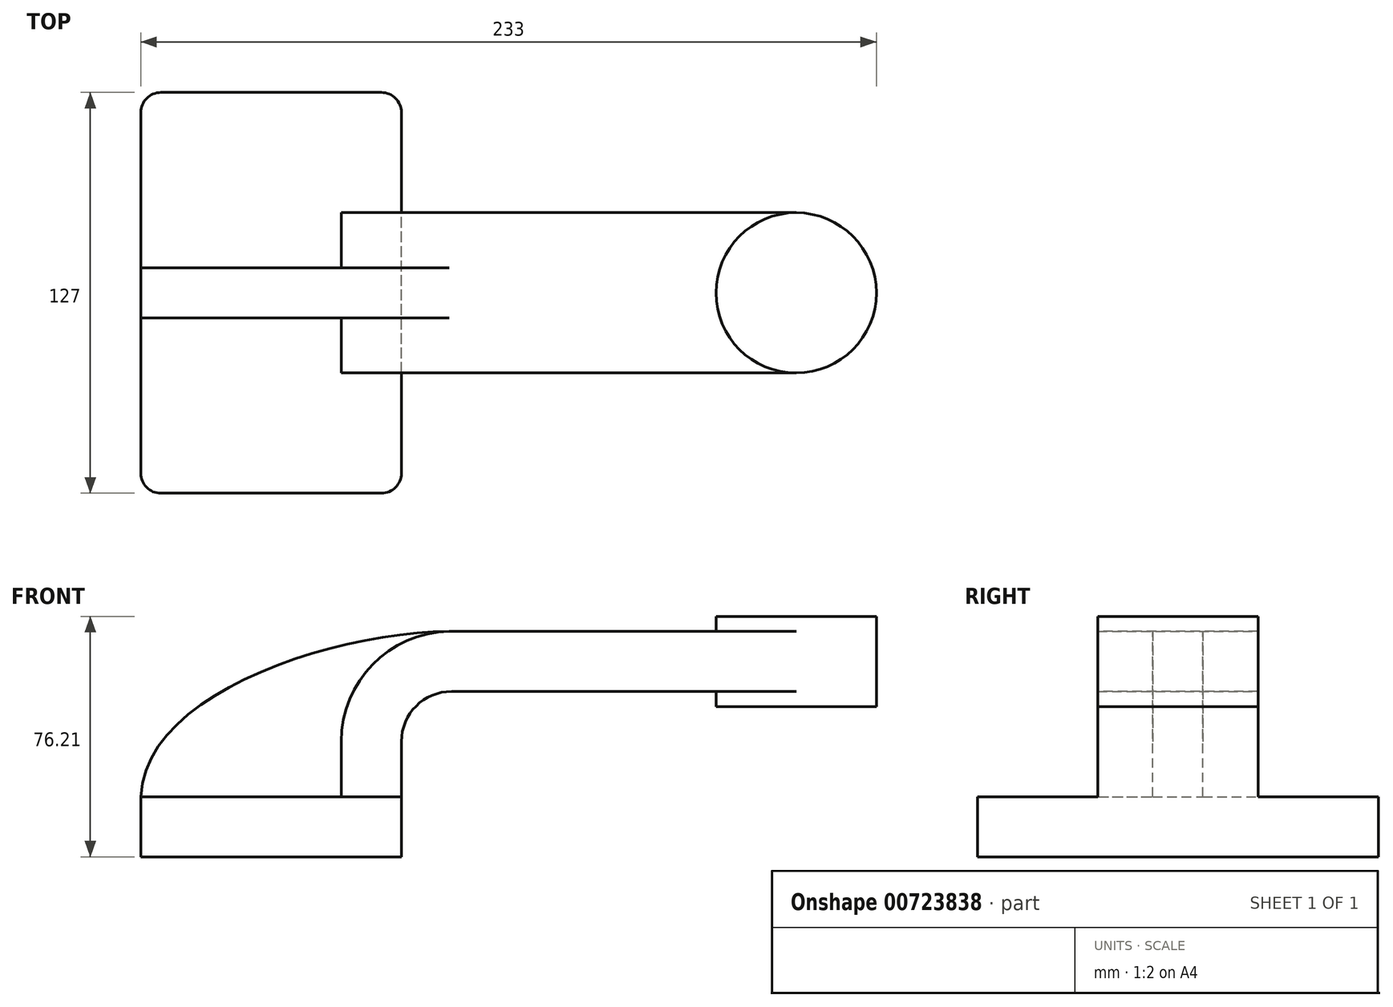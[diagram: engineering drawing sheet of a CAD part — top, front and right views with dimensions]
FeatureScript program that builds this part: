
annotation { "Feature Type Name" : "Feature", "Feature Type Description" : "" }
export const myFeature = defineFeature(function(context is Context, id is Id, definition is map)
    precondition{}
    {
        {
            var Q0;
            Q0=qCreatedBy(makeId("Front.planeOp"),FACE);
            var sketch = newSketch(context, id + "F0", { "sketchPlane" : qUnion([Q0])});
            skLineSegment(sketch, "E0.bottom", {"start": v(-41.27, -9.53) * mm, "end": v(41.28, -9.53) * mm});
            skLineSegment(sketch, "E0.top", {"start": v(-41.28, 9.53) * mm, "end": v(41.28, 9.53) * mm});
            skLineSegment(sketch, "E0.left", {"start": v(-41.28, -9.53) * mm, "end": v(-41.28, 9.53) * mm});
            skLineSegment(sketch, "E0.right", {"start": v(41.28, -9.53) * mm, "end": v(41.28, 9.53) * mm});
            skPoint(sketch, "E0.middle", {"position": v(0, 0) * mm});
            skLineSegment(sketch, "E1.bottom", {"start": v(140.92, 66.68) * mm, "end": v(191.72, 66.68) * mm});
            skLineSegment(sketch, "E1.top", {"start": v(140.92, 38.1) * mm, "end": v(191.72, 38.1) * mm});
            skLineSegment(sketch, "E1.left", {"start": v(140.92, 66.68) * mm, "end": v(140.92, 38.1) * mm});
            skLineSegment(sketch, "E1.right", {"start": v(191.72, 66.68) * mm, "end": v(191.72, 38.1) * mm});
            skPoint(sketch, "E1.middle", {"position": v(166.32, 52.39) * mm});
            skLineSegment(sketch, "E2", {"start": v(41.27, 9.52) * mm, "end": v(41.27, 27) * mm});
            skArc(sketch, "E3", {"start": v(41.27, 27) * mm, "mid": v(45.92, 38.23) * mm, "end": v(57.15, 42.88) * mm});
            skLineSegment(sketch, "E4", {"start": v(57.15, 42.88) * mm, "end": v(166.32, 42.88) * mm});
            skLineSegment(sketch, "E5.0", {"start": v(57.15, 61.93) * mm, "end": v(166.32, 61.93) * mm});
            skArc(sketch, "E5.1", {"start": v(22.22, 27) * mm, "mid": v(32.45, 51.7) * mm, "end": v(57.15, 61.93) * mm});
            skLineSegment(sketch, "E5.2", {"start": v(22.22, 9.52) * mm, "end": v(22.22, 27) * mm});
            skLineSegment(sketch, "E6", {"start": v(166.32, 66.68) * mm, "end": v(166.32, 38.1) * mm});
            skFitSpline(sketch, "E7", {"points": [v(-41.28, 9.53) * mm, v(57.15, 61.93) * mm], "startDerivative": vector(4.1, 99.74) * mm, "endDerivative": vector(111.61, 0.89) * mm});
            skSolve(sketch);
        }
        {
            var Q0;
            Q0=makeQuery(id+"F0.imprint","IMPRINT",FACE,{"disambiguationData":[TD([[makeQuery(id+"F0.imprint","IMPRINT",EDGE,{"derivedFrom":sQuery(id+"F0.wireOp",EDGE,"E0.bottom")}),1.0]])]});
            extrude(context, id + "F1", {"entities" : qUnion([Q0]), "endBound" : BoundingType.SYMMETRIC, "depth" : 127 * mm, "offsetDistance" : 25.4 * mm});
        }
        {
            var Q0;
            {var subQ3=sQuery(id+"F0.wireOp",EDGE,"E5.2");Q0=makeQuery(id+"F0.imprint","IMPRINT",FACE,{"disambiguationData":[TD([[makeQuery(id+"F0.imprint","IMPRINT",EDGE,{"derivedFrom":subQ3}),1.0]])]});}
            extrude(context, id + "F2", {"entities" : qUnion([Q0]), "endBound" : BoundingType.SYMMETRIC, "depth" : 15.88 * mm, "offsetDistance" : 25.4 * mm});
        }
        {
            var Q0;
            {var subQ1=sQuery(id+"F0.wireOp",EDGE,"E2");Q0=makeQuery(id+"F0.imprint","IMPRINT",FACE,{"disambiguationData":[TD([[makeQuery(id+"F0.imprint","IMPRINT",EDGE,{"derivedFrom":subQ1}),1.0]])]});}
            var Q1;
            {var subQ0=sQuery(id+"F0.wireOp",EDGE,"E5.0");var subQ1=sQuery(id+"F0.wireOp",EDGE,"E1.left");var subQ2=makeQuery(id+"F0.imprint","INTERSECT",VERTEX,{"derivedFrom":[subQ1,subQ0]});Q1=makeQuery(id+"F0.imprint","IMPRINT",FACE,{"disambiguationData":[TD([[makeQuery(id+"F0.imprint","IMPRINT",EDGE,{"disambiguationData":[TD([[subQ2,-1.0]])],"derivedFrom":subQ1}),1.0]])]});}
            extrude(context, id + "F3", {"entities" : qUnion([Q0, Q1]), "operationType" : NewBodyOperationType.ADD, "endBound" : BoundingType.SYMMETRIC, "depth" : 50.8 * mm, "offsetDistance" : 25.4 * mm});
        }
        {
            var Q0;
            {var subQ4=sQuery(id+"F0.wireOp",EDGE,"E1.right");Q0=makeQuery(id+"F0.imprint","IMPRINT",FACE,{"disambiguationData":[TD([[makeQuery(id+"F0.imprint","IMPRINT",EDGE,{"derivedFrom":subQ4}),-1.0]])]});}
            var Q1;
            Q1=sQuery(id+"F0.wireOp",EDGE,"E6");
            revolve(context, id + "F4", {"operationType" : NewBodyOperationType.ADD, "surfaceOperationType" : NewSurfaceOperationType.NEW, "entities" : qUnion([Q0]), "axis" : qUnion([Q1]), "revolveType" : RevolveType.FULL});
        }
        {
            var Q0;
            Q0=makeQuery(id+"F1.opExtrude","CAP_EDGE",EDGE,{"disambiguationData":[OSD([sQuery(id+"F0.wireOp",EDGE,"E0.right")])],"isStart":false});
            var Q1;
            Q1=makeQuery(id+"F1.opExtrude","CAP_EDGE",EDGE,{"disambiguationData":[OSD([sQuery(id+"F0.wireOp",EDGE,"E0.left")])],"isStart":false});
            var Q2;
            Q2=makeQuery(id+"F1.opExtrude","CAP_EDGE",EDGE,{"disambiguationData":[OSD([sQuery(id+"F0.wireOp",EDGE,"E0.left")])],"isStart":true});
            var Q3;
            Q3=makeQuery(id+"F1.opExtrude","CAP_EDGE",EDGE,{"disambiguationData":[OSD([sQuery(id+"F0.wireOp",EDGE,"E0.right")])],"isStart":true});
            fillet(context, id + "F5", {"entities" : qUnion([Q0, Q1, Q2, Q3]), "radius" : 6.35 * mm, "tangentPropagation" : true, "allowEdgeOverflow" : false});
        }
    });
